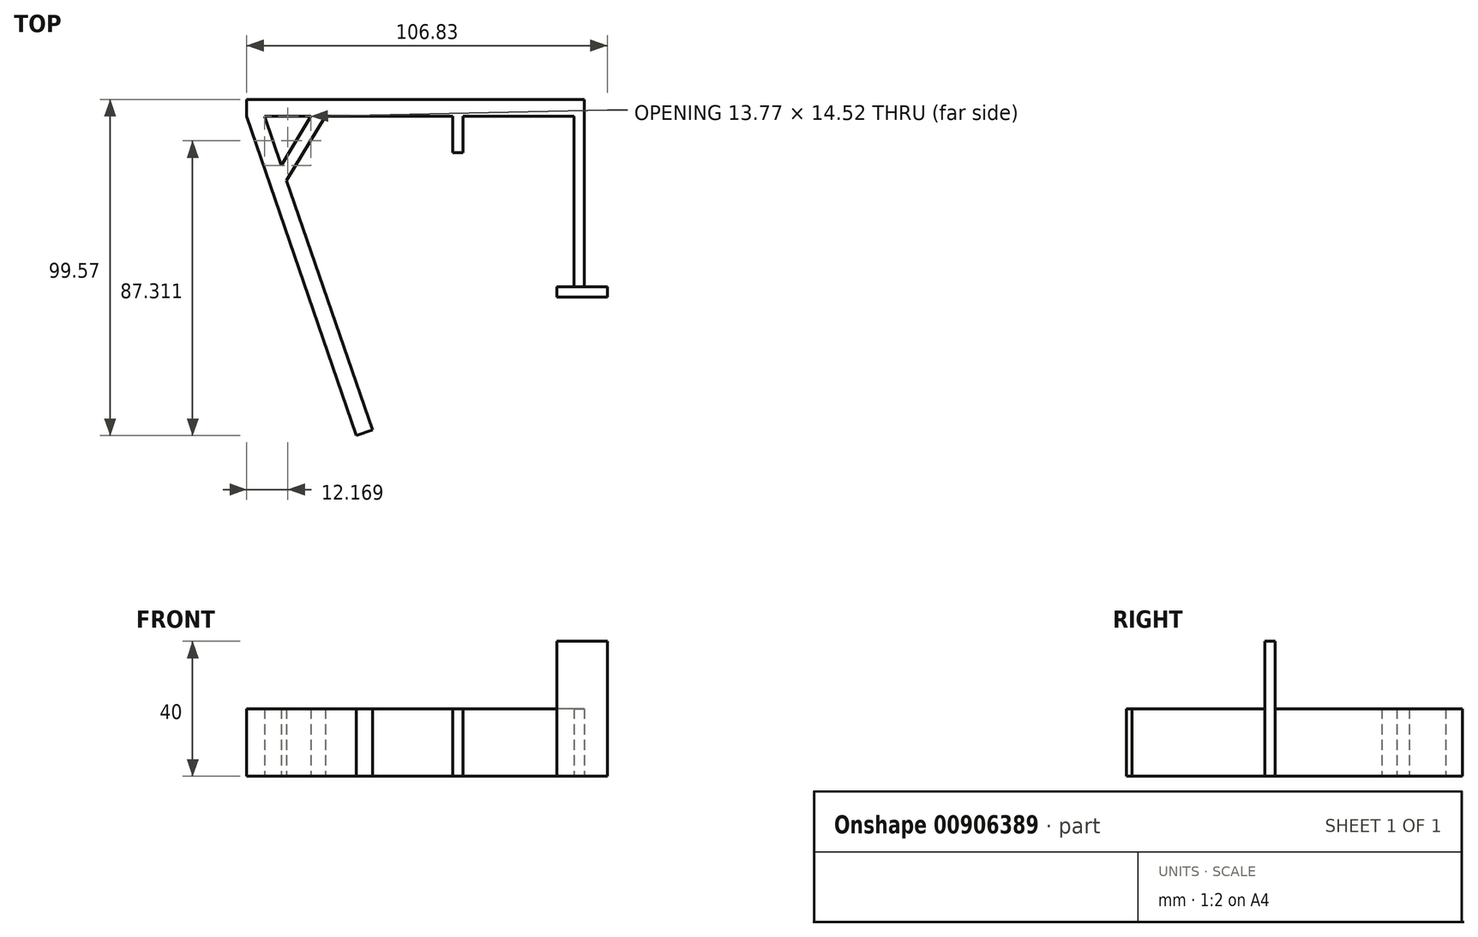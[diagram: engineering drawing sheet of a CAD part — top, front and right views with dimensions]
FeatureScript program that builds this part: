
annotation { "Feature Type Name" : "Feature", "Feature Type Description" : "" }
export const myFeature = defineFeature(function(context is Context, id is Id, definition is map)
    precondition{}
    {
        {
            var Q0;
            Q0=qCreatedBy(makeId("Top.planeOp"),FACE);
            var sketch = newSketch(context, id + "F0", { "sketchPlane" : qUnion([Q0])});
            skLineSegment(sketch, "E0.bottom", {"start": v(0, 0) * mm, "end": v(3, 0) * mm});
            skLineSegment(sketch, "E0.top", {"start": v(0, -50.54) * mm, "end": v(3, -50.54) * mm});
            skLineSegment(sketch, "E0.left", {"start": v(0, 0) * mm, "end": v(0, -50.54) * mm});
            skLineSegment(sketch, "E0.right", {"start": v(3, 0) * mm, "end": v(3, -50.54) * mm});
            skLineSegment(sketch, "E1.bottom", {"start": v(3, 0) * mm, "end": v(-97, 0) * mm});
            skLineSegment(sketch, "E1.top", {"start": v(3, 5) * mm, "end": v(-97, 5) * mm});
            skLineSegment(sketch, "E1.left", {"start": v(3, 0) * mm, "end": v(3, 5) * mm});
            skLineSegment(sketch, "E1.right", {"start": v(-97, 0) * mm, "end": v(-97, 5) * mm});
            skLineSegment(sketch, "E2.bottom", {"start": v(-35.93, 0) * mm, "end": v(-32.93, 0) * mm});
            skLineSegment(sketch, "E2.top", {"start": v(-35.93, -10.72) * mm, "end": v(-32.93, -10.72) * mm});
            skLineSegment(sketch, "E2.left", {"start": v(-35.93, 0) * mm, "end": v(-35.93, -10.72) * mm});
            skLineSegment(sketch, "E2.right", {"start": v(-32.93, 0) * mm, "end": v(-32.93, -10.72) * mm});
            skLineSegment(sketch, "E3", {"start": v(-97, 0) * mm, "end": v(-64.5, -94.57) * mm});
            skLineSegment(sketch, "E4", {"start": v(-64.5, -94.57) * mm, "end": v(-59.77, -92.95) * mm});
            skLineSegment(sketch, "E5", {"start": v(-59.77, -92.95) * mm, "end": v(-91.71, 0) * mm});
            skLineSegment(sketch, "E6", {"start": v(-86.72, -14.52) * mm, "end": v(-77.95, 0) * mm});
            skLineSegment(sketch, "E7", {"start": v(-77.95, 0) * mm, "end": v(-73.73, 0) * mm});
            skLineSegment(sketch, "E8", {"start": v(-73.73, 0) * mm, "end": v(-85.2, -18.96) * mm});
            skSolve(sketch);
        }
        {
            var Q0;
            Q0 = qSketchRegion(id + "F0", true);
            extrude(context, id + "F1", {"entities" : qUnion([Q0]), "depth" : 20 * mm, "offsetDistance" : 25 * mm});
        }
        {
            var Q0;
            Q0=makeQuery(id+"F1.opExtrude","SWEPT_FACE",FACE,{"disambiguationData":[OSD([sQuery(id+"F0.wireOp",EDGE,"E0.top")])]});
            var sketch = newSketch(context, id + "F2", { "sketchPlane" : qUnion([Q0])});
            skLineSegment(sketch, "E9.bottom", {"start": v(-5.17, 0) * mm, "end": v(9.83, 0) * mm});
            skLineSegment(sketch, "E9.top", {"start": v(-5.17, 40) * mm, "end": v(9.83, 40) * mm});
            skLineSegment(sketch, "E9.left", {"start": v(-5.17, 0) * mm, "end": v(-5.17, 40) * mm});
            skLineSegment(sketch, "E9.right", {"start": v(9.83, 0) * mm, "end": v(9.83, 40) * mm});
            skSolve(sketch);
        }
        {
            var Q0;
            Q0 = qSketchRegion(id + "F2", true);
            extrude(context, id + "F3", {"entities" : qUnion([Q0]), "operationType" : NewBodyOperationType.ADD, "depth" : 3 * mm, "offsetDistance" : 25 * mm});
        }
    });
